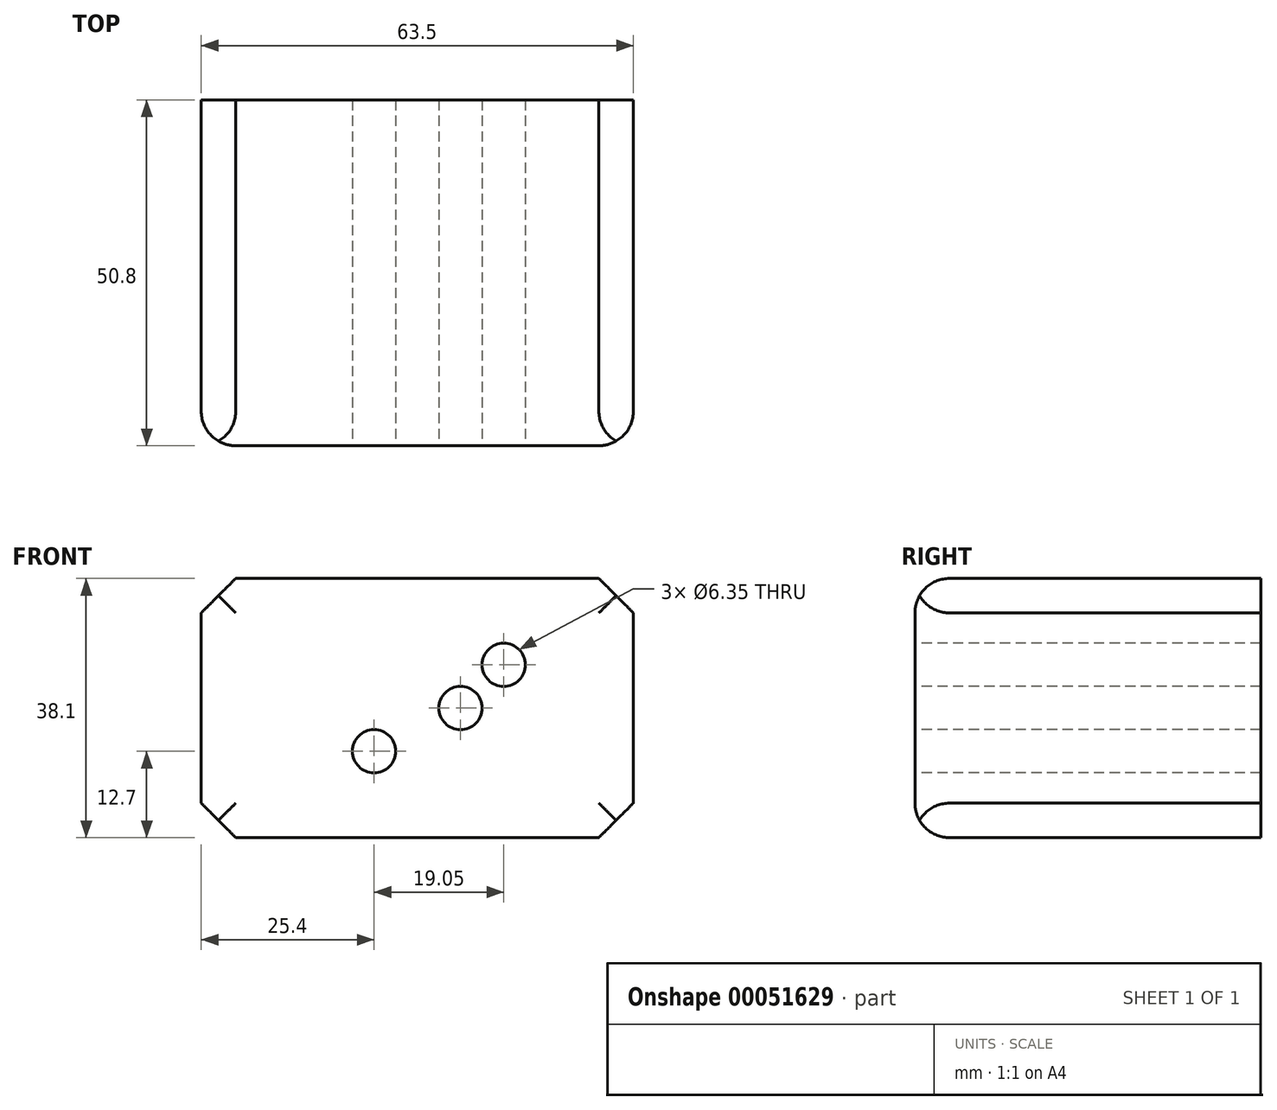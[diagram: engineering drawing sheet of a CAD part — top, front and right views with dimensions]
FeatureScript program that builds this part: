
annotation { "Feature Type Name" : "Feature", "Feature Type Description" : "" }
export const myFeature = defineFeature(function(context is Context, id is Id, definition is map)
    precondition{}
    {
        {
            var Q0;
            Q0=qCreatedBy(makeId("Front.planeOp"),FACE);
            var sketch = newSketch(context, id + "F0", { "sketchPlane" : qUnion([Q0])});
            skLineSegment(sketch, "E0.bottom", {"start": v(0, 0) * mm, "end": v(63.5, 0) * mm});
            skLineSegment(sketch, "E0.top", {"start": v(0, 38.1) * mm, "end": v(63.5, 38.1) * mm});
            skLineSegment(sketch, "E0.left", {"start": v(0, 0) * mm, "end": v(0, 38.1) * mm});
            skLineSegment(sketch, "E0.right", {"start": v(63.5, 0) * mm, "end": v(63.5, 38.1) * mm});
            skSolve(sketch);
        }
        {
            var Q0;
            Q0=makeQuery(id+"F0.imprint","IMPRINT",FACE,{"disambiguationData":[TD([[makeQuery(id+"F0.imprint","IMPRINT",EDGE,{"derivedFrom":sQuery(id+"F0.wireOp",EDGE,"E0.bottom")}),1.0]])]});
            extrude(context, id + "F1", {"entities" : qUnion([Q0]), "oppositeDirection" : true, "depth" : 50.8 * mm});
        }
        {
            var Q0;
            Q0=makeQuery(id+"F1.opExtrude","SWEPT_EDGE",EDGE,{"disambiguationData":[OSD([sQuery(id+"F0.wireOp",EDGE,"E0.top"),sQuery(id+"F0.wireOp",EDGE,"E0.right")])]});
            var Q1;
            Q1=makeQuery(id+"F1.opExtrude","SWEPT_EDGE",EDGE,{"disambiguationData":[OSD([sQuery(id+"F0.wireOp",EDGE,"E0.top"),sQuery(id+"F0.wireOp",EDGE,"E0.left")])]});
            var Q2;
            Q2=makeQuery(id+"F1.opExtrude","SWEPT_EDGE",EDGE,{"disambiguationData":[OSD([sQuery(id+"F0.wireOp",EDGE,"E0.bottom"),sQuery(id+"F0.wireOp",EDGE,"E0.right")])]});
            var Q3;
            Q3=makeQuery(id+"F1.opExtrude","SWEPT_EDGE",EDGE,{"disambiguationData":[OSD([sQuery(id+"F0.wireOp",EDGE,"E0.bottom"),sQuery(id+"F0.wireOp",EDGE,"E0.left")])]});
            chamfer(context, id + "F2", {"entities" : qUnion([Q0, Q1, Q2, Q3]), "width" : 5.08 * mm, "tangentPropagation" : true});
        }
        {
            var Q0;
            Q0=makeQuery(id+"F1.opExtrude","CAP_EDGE",EDGE,{"disambiguationData":[OSD([sQuery(id+"F0.wireOp",EDGE,"E0.right")])],"isStart":true});
            var Q1;
            Q1=makeQuery(id+"F1.opExtrude","CAP_EDGE",EDGE,{"disambiguationData":[OSD([sQuery(id+"F0.wireOp",EDGE,"E0.left")])],"isStart":true});
            var Q2;
            Q2=makeQuery(id+"F1.opExtrude","CAP_EDGE",EDGE,{"disambiguationData":[OSD([sQuery(id+"F0.wireOp",EDGE,"E0.bottom")])],"isStart":true});
            var Q3;
            Q3=makeQuery(id+"F1.opExtrude","CAP_EDGE",EDGE,{"disambiguationData":[OSD([sQuery(id+"F0.wireOp",EDGE,"E0.top")])],"isStart":true});
            fillet(context, id + "F3", {"entities" : qUnion([Q0, Q1, Q2, Q3]), "radius" : 5.08 * mm, "tangentPropagation" : true, "allowEdgeOverflow" : false});
        }
        {
            var Q0;
            Q0=makeQuery(id+"F1.opExtrude","CAP_FACE",FACE,{"disambiguationData":[OSD([sQuery(id+"F0.wireOp",EDGE,"E0.bottom"),sQuery(id+"F0.wireOp",EDGE,"E0.top"),sQuery(id+"F0.wireOp",EDGE,"E0.left"),sQuery(id+"F0.wireOp",EDGE,"E0.right")])],"isStart":true});
            var sketch = newSketch(context, id + "F4", { "sketchPlane" : qUnion([Q0])});
            skPoint(sketch, "E1", {"position": v(25.4, 12.7) * mm});
            skPoint(sketch, "E2", {"position": v(38.1, 19.05) * mm});
            skPoint(sketch, "E3", {"position": v(44.45, 25.4) * mm});
            skSolve(sketch);
        }
        {
            var Q0;
            Q0=sQuery(id+"F4.wireOp",VERTEX,"E1");
            var Q1;
            Q1=sQuery(id+"F4.wireOp",VERTEX,"E3");
            var Q2;
            Q2=sQuery(id+"F4.wireOp",VERTEX,"E2");
            var Q3;
            Q3=makeQuery(id+"F1.opExtrude","SWEPT_BODY",BODY,{"disambiguationData":[OSD([sQuery(id+"F0.wireOp",EDGE,"E0.bottom"),sQuery(id+"F0.wireOp",EDGE,"E0.top"),sQuery(id+"F0.wireOp",EDGE,"E0.left"),sQuery(id+"F0.wireOp",EDGE,"E0.right")])]});
            hole(context, id + "F5", {"style" : HoleStyle.SIMPLE, "holeDiameter" : 6.35 * mm, "endStyle" : HoleEndStyle.THROUGH, "locations" : qUnion([Q0, Q1, Q2]), "scope" : qUnion([Q3])});
        }
        {
            var Q0;
            Q0=makeQuery(id+"F1.opExtrude","SWEPT_BODY",BODY,{"disambiguationData":[OSD([sQuery(id+"F0.wireOp",EDGE,"E0.bottom"),sQuery(id+"F0.wireOp",EDGE,"E0.top"),sQuery(id+"F0.wireOp",EDGE,"E0.left"),sQuery(id+"F0.wireOp",EDGE,"E0.right")])]});
            transform(context, id + "F6", {"entities" : qUnion([Q0]), "transformType" : TransformType.TRANSLATION_3D, "dx" : 50.8 * mm, "dy" : 50.8 * mm, "dz" : 50.8 * mm, "makeCopy" : true});
        }
        {
            var Q0;
            Q0=makeQuery(id+"F6.opPattern","COPY",BODY,{"derivedFrom":makeQuery(id+"F1.opExtrude","SWEPT_BODY",BODY,{"disambiguationData":[OSD([sQuery(id+"F0.wireOp",EDGE,"E0.bottom"),sQuery(id+"F0.wireOp",EDGE,"E0.top"),sQuery(id+"F0.wireOp",EDGE,"E0.left"),sQuery(id+"F0.wireOp",EDGE,"E0.right")])]}),"instanceName":"1"});
            deleteBodies(context, id + "F7", {"entities" : qUnion([Q0])});
        }
    });
